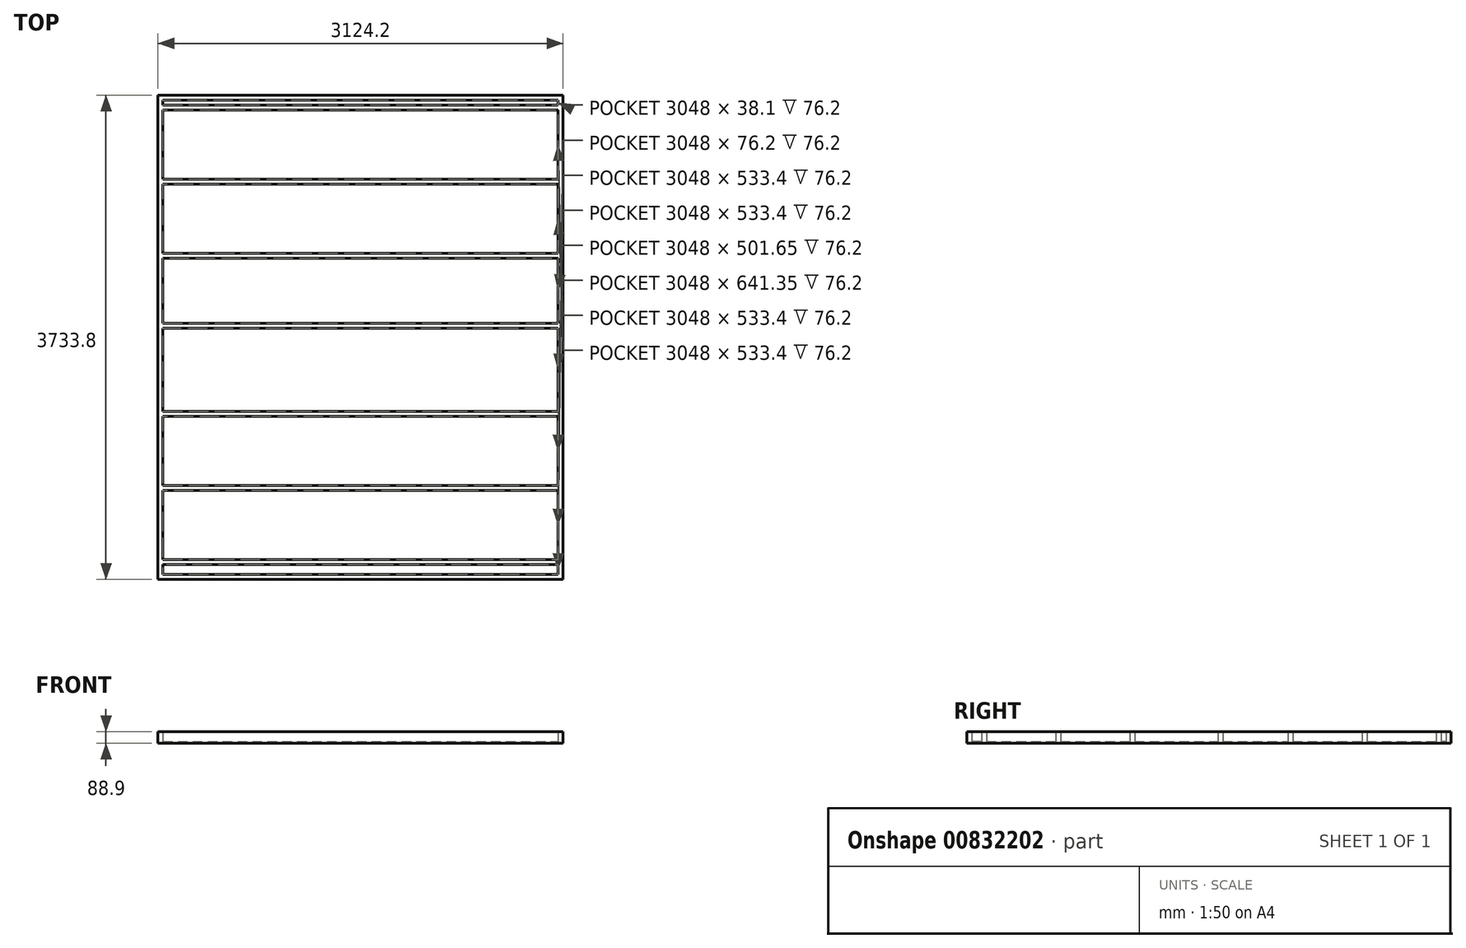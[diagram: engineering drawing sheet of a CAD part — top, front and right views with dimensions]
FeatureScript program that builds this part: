
annotation { "Feature Type Name" : "Feature", "Feature Type Description" : "" }
export const myFeature = defineFeature(function(context is Context, id is Id, definition is map)
    precondition{}
    {
        {
            var Q0;
            Q0=qCreatedBy(makeId("Top.planeOp"),FACE);
            var sketch = newSketch(context, id + "F0", { "sketchPlane" : qUnion([Q0])});
            skLineSegment(sketch, "E0.bottom", {"start": v(1562.1, 1866.9) * mm, "end": v(-1562.1, 1866.9) * mm});
            skLineSegment(sketch, "E0.top", {"start": v(1562.1, -1866.9) * mm, "end": v(-1562.1, -1866.9) * mm});
            skLineSegment(sketch, "E0.left", {"start": v(1562.1, 1866.9) * mm, "end": v(1562.1, -1866.9) * mm});
            skLineSegment(sketch, "E0.right", {"start": v(-1562.1, 1866.9) * mm, "end": v(-1562.1, -1866.9) * mm});
            skPoint(sketch, "E0.middle", {"position": v(0, 0) * mm});
            skSolve(sketch);
        }
        {
            var Q0;
            Q0=qSketchRegion(id+"F0",true);
            extrude(context, id + "F1", {"entities" : qUnion([Q0]), "depth" : 12.7 * mm, "offsetDistance" : 25.4 * mm});
        }
        {
            var Q0;
            Q0=makeQuery(id+"F1.opExtrude","CAP_FACE",FACE,{"disambiguationData":[OSD([sQuery(id+"F0.wireOp",EDGE,"E0.bottom"),sQuery(id+"F0.wireOp",EDGE,"E0.top"),sQuery(id+"F0.wireOp",EDGE,"E0.left"),sQuery(id+"F0.wireOp",EDGE,"E0.right")])],"isStart":false});
            var sketch = newSketch(context, id + "F2", { "sketchPlane" : qUnion([Q0])});
            skLineSegment(sketch, "E1.bottom", {"start": v(-1562.1, 1866.9) * mm, "end": v(1562.1, 1866.9) * mm});
            skLineSegment(sketch, "E1.top", {"start": v(-1562.1, 1828.8) * mm, "end": v(1562.1, 1828.8) * mm});
            skLineSegment(sketch, "E1.left", {"start": v(-1562.1, 1866.9) * mm, "end": v(-1562.1, 1828.8) * mm});
            skLineSegment(sketch, "E1.right", {"start": v(1562.1, 1866.9) * mm, "end": v(1562.1, 1828.8) * mm});
            skLineSegment(sketch, "E2.bottom", {"start": v(1562.1, 1828.8) * mm, "end": v(1524, 1828.8) * mm});
            skLineSegment(sketch, "E2.top", {"start": v(1562.1, -1828.8) * mm, "end": v(1524, -1828.8) * mm});
            skLineSegment(sketch, "E2.left", {"start": v(1562.1, 1828.8) * mm, "end": v(1562.1, -1828.8) * mm});
            skLineSegment(sketch, "E2.right", {"start": v(1524, 1828.8) * mm, "end": v(1524, -38.1) * mm});
            skLineSegment(sketch, "E3.bottom", {"start": v(1562.1, -1828.8) * mm, "end": v(-1562.1, -1828.8) * mm});
            skLineSegment(sketch, "E3.top", {"start": v(1562.1, -1866.9) * mm, "end": v(-1562.1, -1866.9) * mm});
            skLineSegment(sketch, "E3.left", {"start": v(1562.1, -1828.8) * mm, "end": v(1562.1, -1866.9) * mm});
            skLineSegment(sketch, "E3.right", {"start": v(-1562.1, -1828.8) * mm, "end": v(-1562.1, -1866.9) * mm});
            skLineSegment(sketch, "E4.bottom", {"start": v(-1562.1, -1828.8) * mm, "end": v(-1524, -1828.8) * mm});
            skLineSegment(sketch, "E4.top", {"start": v(-1562.1, 1828.8) * mm, "end": v(-1524, 1828.8) * mm});
            skLineSegment(sketch, "E4.left", {"start": v(-1562.1, -1828.8) * mm, "end": v(-1562.1, 1828.8) * mm});
            skLineSegment(sketch, "E5.bottom", {"start": v(-1524, 1219.2) * mm, "end": v(1524, 1219.2) * mm});
            skLineSegment(sketch, "E5.top", {"start": v(-1524, 1181.1) * mm, "end": v(1524, 1181.1) * mm});
            skLineSegment(sketch, "E5.left", {"start": v(-1524, 1219.2) * mm, "end": v(-1524, 1181.1) * mm});
            skLineSegment(sketch, "E5.right", {"start": v(1524, 1219.2) * mm, "end": v(1524, 1181.1) * mm});
            skLineSegment(sketch, "E6.bottom", {"start": v(-1524, 647.7) * mm, "end": v(1524, 647.7) * mm});
            skLineSegment(sketch, "E6.top", {"start": v(-1524, 609.6) * mm, "end": v(1524, 609.6) * mm});
            skLineSegment(sketch, "E6.left", {"start": v(-1524, 647.7) * mm, "end": v(-1524, 609.6) * mm});
            skLineSegment(sketch, "E6.right", {"start": v(1524, 647.7) * mm, "end": v(1524, 609.6) * mm});
            skLineSegment(sketch, "E7.bottom", {"start": v(-1524, -571.5) * mm, "end": v(1524, -571.5) * mm});
            skLineSegment(sketch, "E7.top", {"start": v(-1524, -609.6) * mm, "end": v(1524, -609.6) * mm});
            skLineSegment(sketch, "E7.left", {"start": v(-1524, -571.5) * mm, "end": v(-1524, -609.6) * mm});
            skLineSegment(sketch, "E7.right", {"start": v(1524, -571.5) * mm, "end": v(1524, -609.6) * mm});
            skLineSegment(sketch, "E8.bottom", {"start": v(-1524, -1143) * mm, "end": v(1524, -1143) * mm});
            skLineSegment(sketch, "E8.top", {"start": v(-1524, -1181.1) * mm, "end": v(1524, -1181.1) * mm});
            skLineSegment(sketch, "E8.left", {"start": v(-1524, -1143) * mm, "end": v(-1524, -1181.1) * mm});
            skLineSegment(sketch, "E8.right", {"start": v(1524, -1143) * mm, "end": v(1524, -1181.1) * mm});
            skLineSegment(sketch, "E9.bottom", {"start": v(1524, -1714.5) * mm, "end": v(-1524, -1714.5) * mm});
            skLineSegment(sketch, "E9.top", {"start": v(1524, -1752.6) * mm, "end": v(-1524, -1752.6) * mm});
            skLineSegment(sketch, "E9.left", {"start": v(1524, -1714.5) * mm, "end": v(1524, -1752.6) * mm});
            skLineSegment(sketch, "E9.right", {"start": v(-1524, -1714.5) * mm, "end": v(-1524, -1752.6) * mm});
            skLineSegment(sketch, "E10.bottom", {"start": v(-1524, 1790.7) * mm, "end": v(1524, 1790.7) * mm});
            skLineSegment(sketch, "E10.top", {"start": v(-1524, 1752.6) * mm, "end": v(1524, 1752.6) * mm});
            skLineSegment(sketch, "E10.left", {"start": v(-1524, 1790.7) * mm, "end": v(-1524, 1752.6) * mm});
            skLineSegment(sketch, "E10.right", {"start": v(1524, 1790.7) * mm, "end": v(1524, 1752.6) * mm});
            skLineSegment(sketch, "E11", {"start": v(-1524, -1828.8) * mm, "end": v(-1524, 1828.8) * mm});
            skLineSegment(sketch, "E12.trimOffspring", {"start": v(1524, -38.1) * mm, "end": v(1524, -1828.8) * mm});
            skLineSegment(sketch, "E13.bottom", {"start": v(-1524, 107.95) * mm, "end": v(1524, 107.95) * mm});
            skLineSegment(sketch, "E13.top", {"start": v(-1524, 69.85) * mm, "end": v(1524, 69.85) * mm});
            skLineSegment(sketch, "E13.left", {"start": v(-1524, 107.95) * mm, "end": v(-1524, 69.85) * mm});
            skLineSegment(sketch, "E13.right", {"start": v(1524, 107.95) * mm, "end": v(1524, 69.85) * mm});
            skSolve(sketch);
        }
        {
            var Q0;
            Q0=qSketchRegion(id+"F2",true);
            var Q1;
            {var subQ0=sQuery(id+"F2.wireOp",EDGE,"E10.bottom");Q1=makeQuery(id+"F2.imprint","IMPRINT",FACE,{"disambiguationData":[TD([[makeQuery(id+"F2.imprint","IMPRINT",EDGE,{"derivedFrom":subQ0}),-1.0]])]});}
            var Q2;
            {var subQ0=sQuery(id+"F2.wireOp",EDGE,"E5.bottom");Q2=makeQuery(id+"F2.imprint","IMPRINT",FACE,{"disambiguationData":[TD([[makeQuery(id+"F2.imprint","IMPRINT",EDGE,{"derivedFrom":subQ0}),-1.0]])]});}
            var Q3;
            {var subQ0=sQuery(id+"F2.wireOp",EDGE,"E6.bottom");Q3=makeQuery(id+"F2.imprint","IMPRINT",FACE,{"disambiguationData":[TD([[makeQuery(id+"F2.imprint","IMPRINT",EDGE,{"derivedFrom":subQ0}),-1.0]])]});}
            var Q4;
            Q4=makeQuery(id+"F2.imprint","IMPRINT",FACE,{"disambiguationData":[TD([[makeQuery(id+"F2.imprint","IMPRINT",EDGE,{"derivedFrom":sQuery(id+"F2.wireOp",EDGE,"E13.bottom")}),-1.0]])]});
            var Q5;
            {var subQ0=sQuery(id+"F2.wireOp",EDGE,"E7.bottom");Q5=makeQuery(id+"F2.imprint","IMPRINT",FACE,{"disambiguationData":[TD([[makeQuery(id+"F2.imprint","IMPRINT",EDGE,{"derivedFrom":subQ0}),-1.0]])]});}
            var Q6;
            {var subQ0=sQuery(id+"F2.wireOp",EDGE,"E9.bottom");Q6=makeQuery(id+"F2.imprint","IMPRINT",FACE,{"disambiguationData":[TD([[makeQuery(id+"F2.imprint","IMPRINT",EDGE,{"derivedFrom":subQ0}),1.0]])]});}
            var Q7;
            {var subQ0=sQuery(id+"F2.wireOp",EDGE,"E8.bottom");Q7=makeQuery(id+"F2.imprint","IMPRINT",FACE,{"disambiguationData":[TD([[makeQuery(id+"F2.imprint","IMPRINT",EDGE,{"derivedFrom":subQ0}),-1.0]])]});}
            extrude(context, id + "F3", {"entities" : qUnion([Q0, Q1, Q2, Q3, Q4, Q5, Q6, Q7]), "operationType" : NewBodyOperationType.ADD, "depth" : 76.2 * mm, "offsetDistance" : 25.4 * mm});
        }
    });
